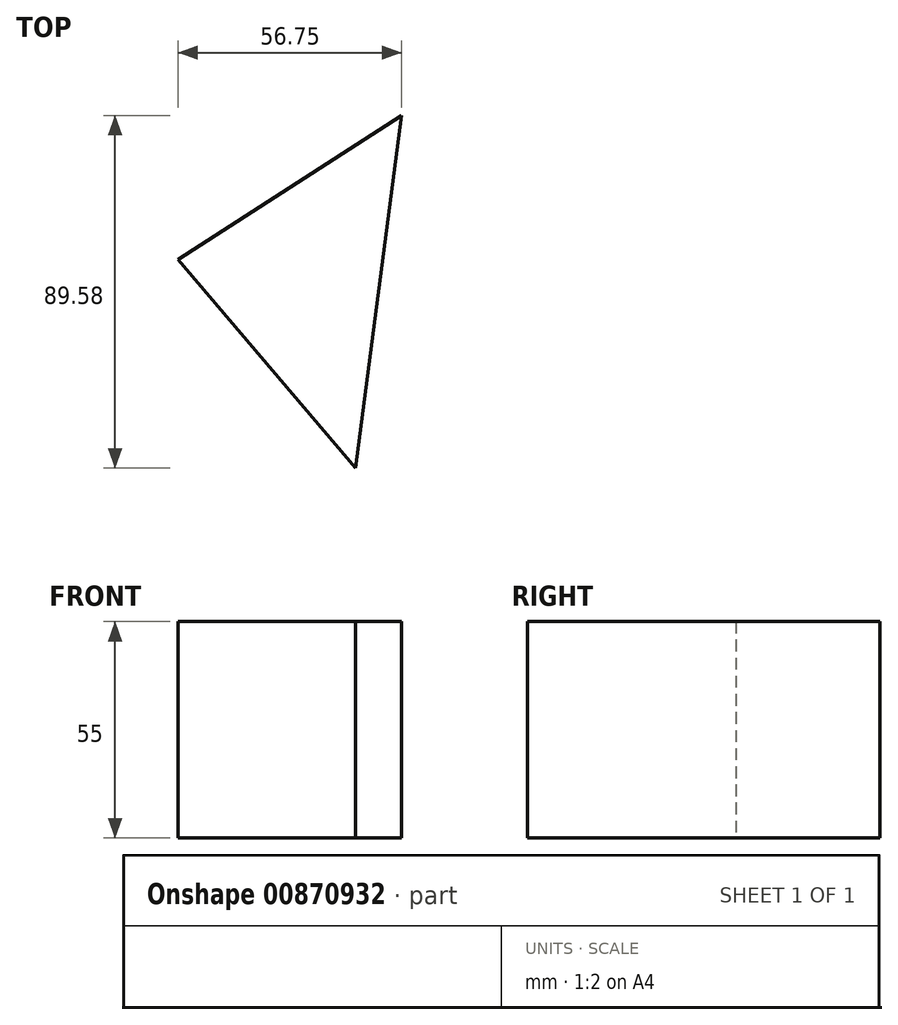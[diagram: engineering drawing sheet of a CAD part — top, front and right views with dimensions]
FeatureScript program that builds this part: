
annotation { "Feature Type Name" : "Feature", "Feature Type Description" : "" }
export const myFeature = defineFeature(function(context is Context, id is Id, definition is map)
    precondition{}
    {
        {
            var Q0;
            Q0=qCreatedBy(makeId("Top.planeOp"),FACE);
            var sketch = newSketch(context, id + "F0", { "sketchPlane" : qUnion([Q0])});
            skLineSegment(sketch, "E0", {"start": v(56.75, 58.1) * mm, "end": v(0, 21.47) * mm});
            skLineSegment(sketch, "E1", {"start": v(0, 21.47) * mm, "end": v(45.04, -31.48) * mm});
            skLineSegment(sketch, "E2", {"start": v(45.04, -31.48) * mm, "end": v(56.75, 58.1) * mm});
            skSolve(sketch);
        }
        {
            var Q0;
            Q0 = qSketchRegion(id + "F0", true);
            extrude(context, id + "F1", {"entities" : qUnion([Q0]), "endBound" : BoundingType.SYMMETRIC, "depth" : 55 * mm, "offsetDistance" : 25.4 * mm});
        }
    });
